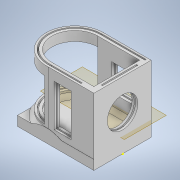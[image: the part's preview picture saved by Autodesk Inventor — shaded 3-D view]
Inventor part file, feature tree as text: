
AUTODESK INVENTOR PART (.ipt)
format: ipt  version: 2022 (Build 260153000, 153)  size: 295,424 bytes
history: native  units: mm
features: sketch x9, extrude x7, projected_geometry x5, plane x1, chamfer x1, hole x1
ambient origin geometry x8: Origin, YZ Plane, XZ Plane, XY Plane, X Axis, Y Axis, Z Axis, Center Point
bodies: Volumenkörper1 (feature_tree)
feature tree (24):
  extrude  "Extrusion1"  Depth=30.0mm
  extrude  "Extrusion2"  Depth=30.0mm
  plane  "Arbeitsebene1"
  extrude  "Extrusion3"  Depth=30.0mm TaperAngle=0.0deg
  extrude  "Extrusion4"  Depth=12.0mm
  extrude  "Extrusion5"  Depth=0.65mm
  chamfer  "Fase1"  Distance=28.0mm
  extrude  "Extrusion6"  Depth=14.0mm
  sketch  "Skizze7"  dims[d17=14.0mm d18=14.0mm]
  extrude  "Extrusion7"  Depth=2.0mm TaperAngle=45.0deg
  hole  "Bohrung1"  [1 undecoded]
  sketch  "Skizze1"  dims[d0=40.0mm d1=30.0mm]
  sketch  "Skizze2"  dims[d2=5.0mm d3=0.0mm d4=30.0mm]
  sketch  "Skizze3"  dims[d6=3.0mm d7=30.0mm d8=0.0mm]
  projected_geometry  "Projizierte Kontur1"
  sketch  "Skizze4"  dims[d9=3.0mm d10=12.0mm]
  projected_geometry  "Projizierte Kontur2"
  sketch  "Skizze5"  dims[d11=22.0mm d12=0.0mm d13=0.65mm]
  projected_geometry  "Projizierte Kontur3"
  sketch  "Skizze6"  dims[d14=1.0mm d15=28.0mm d16=0.0mm]
  projected_geometry  "Projizierte Kontur4"
  sketch  "Skizze8"  dims[d19=3.0mm d20=0.0mm d21=2.0mm d22=2.0mm d23=45.0deg]
  sketch  "Skizze9"  dims[d24=16.0mm d25=3.0mm d26=0.0mm d27=0.7mm d28=18.5mm d29=24.5mm d30=0.0mm d31=7.0mm d32=7.0mm d33=7.0mm d34=4.9mm d35=6.0mm d36=4.0mm d37=2.0mm d38=90.0deg d39=3.5mm d40=20.594885mm d41=5.0mm]
  projected_geometry  "Projizierte Kontur5"
note: 1 required parameter value undecoded (feature->parameter linkage not recoverable at this tier; creation-order binding heuristic only, values carry confidence <= 0.55)
